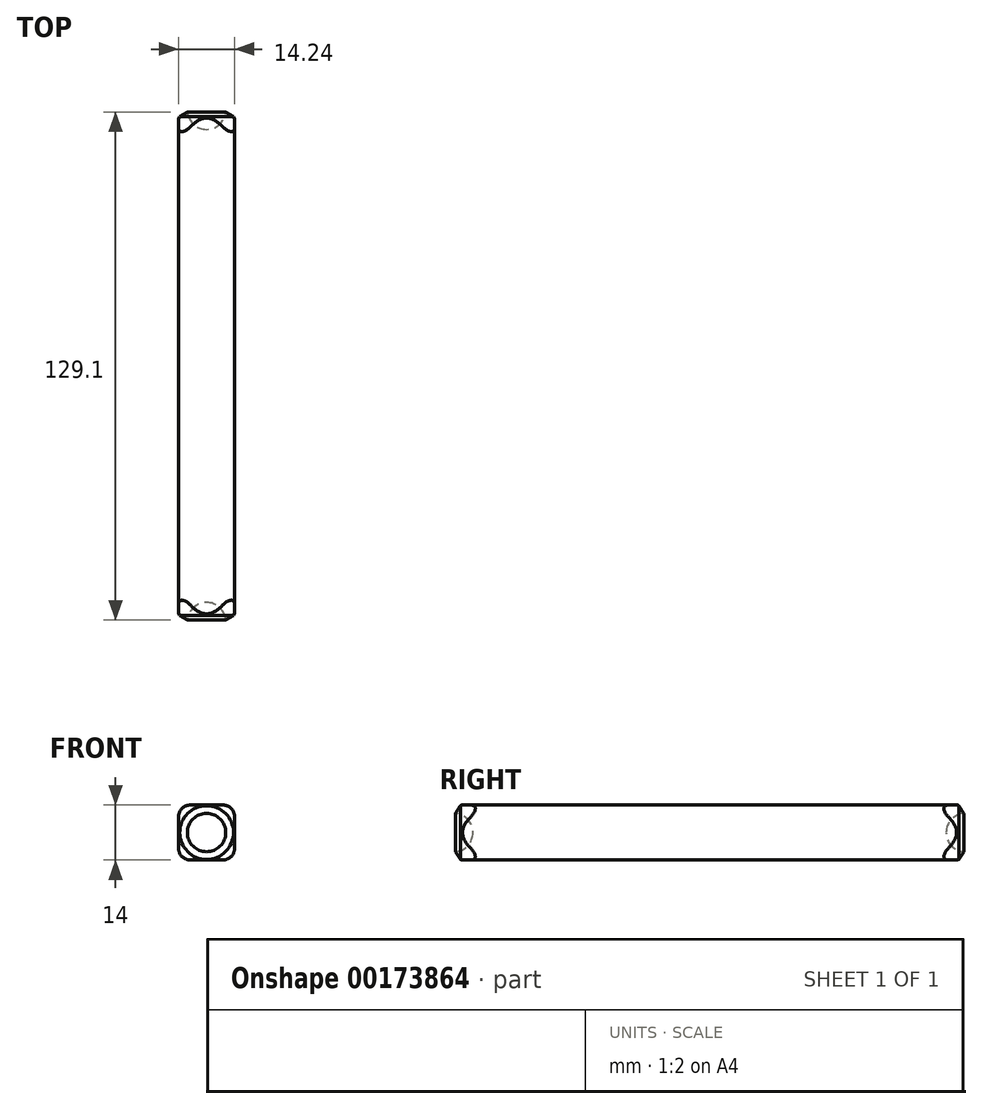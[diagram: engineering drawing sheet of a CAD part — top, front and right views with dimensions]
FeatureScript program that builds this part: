
annotation { "Feature Type Name" : "Feature", "Feature Type Description" : "" }
export const myFeature = defineFeature(function(context is Context, id is Id, definition is map)
    precondition{}
    {
        {
            var Q0;
            Q0=qCreatedBy(makeId("Front.planeOp"),FACE);
            var sketch = newSketch(context, id + "F0", { "sketchPlane" : qUnion([Q0])});
            skLineSegment(sketch, "E0.bottom", {"start": v(-7.12, 7) * mm, "end": v(7.12, 7) * mm});
            skLineSegment(sketch, "E0.top", {"start": v(-7.12, -7) * mm, "end": v(7.12, -7) * mm});
            skLineSegment(sketch, "E0.left", {"start": v(-7.12, 7) * mm, "end": v(-7.12, -7) * mm});
            skLineSegment(sketch, "E0.right", {"start": v(7.12, 7) * mm, "end": v(7.12, -7) * mm});
            skPoint(sketch, "E0.middle", {"position": v(0, 0) * mm});
            skSolve(sketch);
        }
        {
            var Q0;
            Q0=makeQuery(id+"F0.imprint","IMPRINT",FACE,{"disambiguationData":[TD([[makeQuery(id+"F0.imprint","IMPRINT",EDGE,{"derivedFrom":sQuery(id+"F0.wireOp",EDGE,"10765183-696f-45f7-a58a-d9f82d469cdb.0")}),-1.0]])]});
            var Q1;
            Q1=makeQuery(id+"F0.imprint","IMPRINT",FACE,{"disambiguationData":[TD([[makeQuery(id+"F0.imprint","IMPRINT",EDGE,{"derivedFrom":sQuery(id+"F0.wireOp",EDGE,"E0.bottom")}),-1.0]])]});
            extrude(context, id + "F1", {"entities" : qUnion([Q0, Q1]), "depth" : 65 * mm});
        }
        {
            var Q0;
            Q0=makeQuery(id+"F1.opExtrude","CAP_FACE",FACE,{"disambiguationData":[OSD([sQuery(id+"F0.wireOp",EDGE,"E0.bottom"),sQuery(id+"F0.wireOp",EDGE,"E0.top"),sQuery(id+"F0.wireOp",EDGE,"E0.left"),sQuery(id+"F0.wireOp",EDGE,"E0.right")])],"isStart":false});
            var sketch = newSketch(context, id + "F2", { "sketchPlane" : qUnion([Q0])});
            skCircle(sketch, "E1", {"center": v(0, 0) * mm, "radius": 4.9 * mm});
            skCircle(sketch, "E2", {"center": v(0, 0) * mm, "radius": 6 * mm});
            skLineSegment(sketch, "E3", {"start": v(-4.9, 0) * mm, "end": v(4.9, 0) * mm});
            skSolve(sketch);
        }
        {
            var Q0;
            {var subQ0=sQuery(id+"F2.wireOp",EDGE,"E3");Q0=makeQuery(id+"F2.imprint","IMPRINT",FACE,{"disambiguationData":[TD([[makeQuery(id+"F2.imprint","IMPRINT",EDGE,{"derivedFrom":subQ0}),-1.0]])]});}
            var Q1;
            Q1=sQuery(id+"F2.wireOp",EDGE,"E3");
            revolve(context, id + "F3", {"operationType" : NewBodyOperationType.REMOVE, "entities" : qUnion([Q0]), "axis" : qUnion([Q1]), "revolveType" : RevolveType.FULL, "oppositeDirection" : true});
        }
        {
            var Q0;
            Q0=makeQuery(id+"F2.imprint","IMPRINT",FACE,{"disambiguationData":[TD([[makeQuery(id+"F2.imprint","IMPRINT",EDGE,{"derivedFrom":sQuery(id+"F2.wireOp",EDGE,"E2")}),-1.0]])]});
            extrude(context, id + "F4", {"entities" : qUnion([Q0]), "operationType" : NewBodyOperationType.REMOVE, "oppositeDirection" : true, "depth" : 6 * mm});
        }
        {
            var Q0;
            Q0=makeQuery(id+"F1.opExtrude","SWEPT_EDGE",EDGE,{"disambiguationData":[OSD([sQuery(id+"F0.wireOp",EDGE,"E0.bottom"),sQuery(id+"F0.wireOp",EDGE,"E0.left")])]});
            var Q1;
            Q1=makeQuery(id+"F1.opExtrude","SWEPT_EDGE",EDGE,{"disambiguationData":[OSD([sQuery(id+"F0.wireOp",EDGE,"E0.top"),sQuery(id+"F0.wireOp",EDGE,"E0.left")])]});
            var Q2;
            Q2=makeQuery(id+"F1.opExtrude","SWEPT_EDGE",EDGE,{"disambiguationData":[OSD([sQuery(id+"F0.wireOp",EDGE,"E0.top"),sQuery(id+"F0.wireOp",EDGE,"E0.right")])]});
            var Q3;
            Q3=makeQuery(id+"F1.opExtrude","SWEPT_EDGE",EDGE,{"disambiguationData":[OSD([sQuery(id+"F0.wireOp",EDGE,"E0.bottom"),sQuery(id+"F0.wireOp",EDGE,"E0.right")])]});
            fillet(context, id + "F5", {"entities" : qUnion([Q0, Q1, Q2, Q3]), "radius" : 3 * mm, "tangentPropagation" : true, "allowEdgeOverflow" : false});
        }
        {
            var Q0;
            Q0=makeQuery(id+"F4.boolean.opBoolean","COPY",EDGE,{"derivedFrom":makeQuery(id+"F4.opExtrude","CAP_EDGE",EDGE,{"disambiguationData":[OSD([sQuery(id+"F2.wireOp",EDGE,"E2")])],"isStart":false})});
            chamfer(context, id + "F6", {"entities" : qUnion([Q0]), "chamferType" : ChamferType.TWO_OFFSETS, "width1" : 6 * mm, "oppositeDirection" : false, "width2" : 3 * mm, "tangentPropagation" : true});
        }
        {
            var Q0;
            Q0=makeQuery(id+"F6.opChamfer","BLEND_EDGE",EDGE,{"blendedFrom":[makeQuery(id+"F4.boolean.opBoolean","COPY",EDGE,{"derivedFrom":makeQuery(id+"F4.opExtrude","CAP_EDGE",EDGE,{"disambiguationData":[OSD([sQuery(id+"F2.wireOp",EDGE,"E2")])],"isStart":false})}),makeQuery(id+"F1.opExtrude","CAP_FACE",FACE,{"disambiguationData":[OSD([sQuery(id+"F0.wireOp",EDGE,"E0.bottom"),sQuery(id+"F0.wireOp",EDGE,"E0.top"),sQuery(id+"F0.wireOp",EDGE,"E0.left"),sQuery(id+"F0.wireOp",EDGE,"E0.right")])],"isStart":false})],"blendedInto":[makeQuery(id+"F1.opExtrude","CAP_FACE",FACE,{"disambiguationData":[OSD([sQuery(id+"F0.wireOp",EDGE,"E0.bottom"),sQuery(id+"F0.wireOp",EDGE,"E0.top"),sQuery(id+"F0.wireOp",EDGE,"E0.left"),sQuery(id+"F0.wireOp",EDGE,"E0.right")])],"isStart":false})]});
            chamfer(context, id + "F7", {"entities" : qUnion([Q0]), "width" : 3 * mm, "tangentPropagation" : true});
        }
        {
            var Q0;
            Q0=makeQuery(id+"F1.opExtrude","SWEPT_BODY",BODY,{"disambiguationData":[OSD([sQuery(id+"F0.wireOp",EDGE,"E0.bottom"),sQuery(id+"F0.wireOp",EDGE,"E0.top"),sQuery(id+"F0.wireOp",EDGE,"E0.left"),sQuery(id+"F0.wireOp",EDGE,"E0.right")])]});
            var Q1;
            Q1=makeQuery(id+"F1.opExtrude","CAP_FACE",FACE,{"disambiguationData":[OSD([sQuery(id+"F0.wireOp",EDGE,"E0.bottom"),sQuery(id+"F0.wireOp",EDGE,"E0.top"),sQuery(id+"F0.wireOp",EDGE,"E0.left"),sQuery(id+"F0.wireOp",EDGE,"E0.right")])],"isStart":true});
            mirror(context, id + "F8", {"operationType" : NewBodyOperationType.ADD, "entities" : qUnion([Q0]), "mirrorPlane" : qUnion([Q1])});
        }
    });
